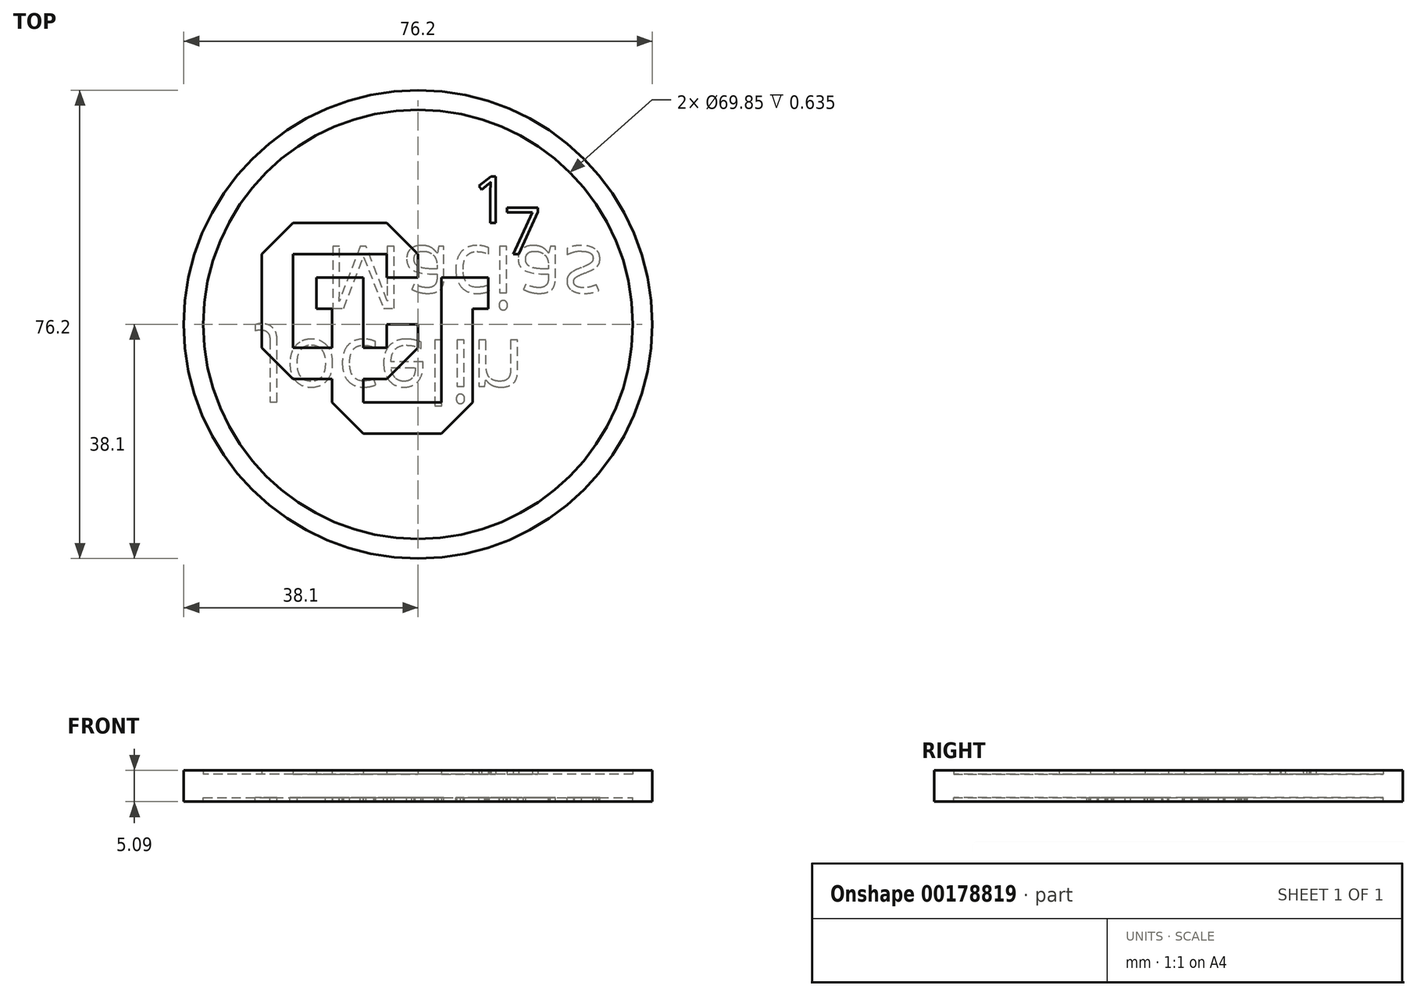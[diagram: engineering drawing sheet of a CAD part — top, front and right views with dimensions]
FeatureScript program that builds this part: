
annotation { "Feature Type Name" : "Feature", "Feature Type Description" : "" }
export const myFeature = defineFeature(function(context is Context, id is Id, definition is map)
    precondition{}
    {
        {
            var Q0;
            Q0=qCreatedBy(makeId("Top.planeOp"),FACE);
            var sketch = newSketch(context, id + "F0", { "sketchPlane" : qUnion([Q0])});
            skCircle(sketch, "E0", {"center": v(0, 0) * mm, "radius": 38.1 * mm});
            skSolve(sketch);
        }
        {
            var Q0;
            Q0=makeQuery(id+"F0.imprint","IMPRINT",FACE,{"disambiguationData":[TD([[makeQuery(id+"F0.imprint","IMPRINT",EDGE,{"derivedFrom":sQuery(id+"F0.wireOp",EDGE,"E0")}),1.0]])]});
            extrude(context, id + "F1", {"entities" : qUnion([Q0]), "depth" : 3.8 * mm});
        }
        {
            var Q0;
            Q0=makeQuery(id+"F1.opExtrude","CAP_FACE",FACE,{"disambiguationData":[OSD([sQuery(id+"F0.wireOp",EDGE,"E0")])],"isStart":false});
            var sketch = newSketch(context, id + "F2", { "sketchPlane" : qUnion([Q0])});
            skLineSegment(sketch, "E1", {"start": v(0, 0) * mm, "end": v(0, -3.81) * mm});
            skLineSegment(sketch, "E2", {"start": v(0, -3.81) * mm, "end": v(-5.08, -8.9) * mm});
            skLineSegment(sketch, "E3", {"start": v(-5.08, -8.9) * mm, "end": v(-8.9, -8.9) * mm});
            skLineSegment(sketch, "E4", {"start": v(-20.32, -8.9) * mm, "end": v(-25.4, -3.81) * mm});
            skLineSegment(sketch, "E5", {"start": v(-25.4, -3.81) * mm, "end": v(-25.4, 11.43) * mm});
            skLineSegment(sketch, "E6", {"start": v(-25.4, 11.43) * mm, "end": v(-20.32, 16.5) * mm});
            skLineSegment(sketch, "E7", {"start": v(-20.32, 16.51) * mm, "end": v(-5.08, 16.51) * mm});
            skLineSegment(sketch, "E8", {"start": v(-5.08, 16.51) * mm, "end": v(0, 11.43) * mm});
            skLineSegment(sketch, "E9", {"start": v(0, 11.43) * mm, "end": v(0, 7.62) * mm});
            skLineSegment(sketch, "E10", {"start": v(0, 7.62) * mm, "end": v(-5.08, 7.62) * mm});
            skLineSegment(sketch, "E11", {"start": v(-5.08, 7.62) * mm, "end": v(-5.08, 11.43) * mm});
            skLineSegment(sketch, "E12", {"start": v(-5.08, 11.43) * mm, "end": v(-20.32, 11.43) * mm});
            skLineSegment(sketch, "E13", {"start": v(-20.32, 11.43) * mm, "end": v(-20.32, -3.81) * mm});
            skLineSegment(sketch, "E14", {"start": v(-20.32, -3.81) * mm, "end": v(-13.97, -3.81) * mm});
            skLineSegment(sketch, "E15", {"start": v(-5.08, -3.81) * mm, "end": v(-5.08, 0) * mm});
            skLineSegment(sketch, "E16", {"start": v(-5.08, 0) * mm, "end": v(0, 0) * mm});
            skLineSegment(sketch, "E17", {"start": v(-8.9, -3.81) * mm, "end": v(-8.9, 7.62) * mm});
            skLineSegment(sketch, "E18", {"start": v(-8.9, 7.62) * mm, "end": v(-16.5, 7.62) * mm});
            skLineSegment(sketch, "E19", {"start": v(-16.5, 7.62) * mm, "end": v(-16.5, 2.54) * mm});
            skLineSegment(sketch, "E20", {"start": v(-16.51, 2.54) * mm, "end": v(-13.97, 2.54) * mm});
            skLineSegment(sketch, "E21", {"start": v(-13.97, 2.54) * mm, "end": v(-13.97, -3.8) * mm});
            skLineSegment(sketch, "E22.trimOffspring", {"start": v(-8.9, -3.81) * mm, "end": v(-5.08, -3.81) * mm});
            skLineSegment(sketch, "E23", {"start": v(-13.97, -12.7) * mm, "end": v(-13.97, -8.9) * mm});
            skLineSegment(sketch, "E24", {"start": v(-13.97, -12.7) * mm, "end": v(-8.9, -17.78) * mm});
            skLineSegment(sketch, "E25", {"start": v(-8.9, -17.78) * mm, "end": v(3.8, -17.78) * mm});
            skLineSegment(sketch, "E26", {"start": v(3.8, -17.78) * mm, "end": v(8.89, -12.7) * mm});
            skLineSegment(sketch, "E27", {"start": v(8.89, -12.7) * mm, "end": v(8.9, 2.54) * mm});
            skLineSegment(sketch, "E28", {"start": v(8.9, 2.54) * mm, "end": v(11.43, 2.54) * mm});
            skLineSegment(sketch, "E29", {"start": v(11.43, 2.54) * mm, "end": v(11.43, 7.62) * mm});
            skLineSegment(sketch, "E30", {"start": v(11.43, 7.62) * mm, "end": v(3.8, 7.62) * mm});
            skLineSegment(sketch, "E31", {"start": v(3.8, 7.62) * mm, "end": v(3.8, -12.7) * mm});
            skLineSegment(sketch, "E32", {"start": v(3.8, -12.7) * mm, "end": v(-8.9, -12.7) * mm});
            skLineSegment(sketch, "E33", {"start": v(-8.9, -12.7) * mm, "end": v(-8.9, -8.9) * mm});
            skLineSegment(sketch, "E34.trimOffspring", {"start": v(-13.97, -8.9) * mm, "end": v(-20.32, -8.9) * mm});
            skCircle(sketch, "E35", {"center": v(0, 0) * mm, "radius": 38.1 * mm});
            skCircle(sketch, "E36.0", {"center": v(0, 0) * mm, "radius": 34.93 * mm});
            skText(sketch, "E37", { "text": "1\n", "fontName": "OpenSans-Regular.ttf"});
            skText(sketch, "E38", { "text": "7\n", "fontName": "OpenSans-Regular.ttf"});
            const initialGuessF2  = {"E37": [0.0089, 0.0165, 1, 0, 0.00762], "E38": [0.01397, 0.01143, 1, 0, 0.00762]};
            skSetInitialGuess(sketch, initialGuessF2);
            skSolve(sketch);
        }
        {
            var Q0;
            Q0=qSketchRegion(id+"F2",true);
            var Q1;
            Q1=makeQuery(id+"F2.imprint","IMPRINT",FACE,{"disambiguationData":[TD([[makeQuery(id+"F2.imprint","IMPRINT",EDGE,{"derivedFrom":sQuery(id+"F2.wireOp",EDGE,"06a9ea4b-25a0-40bb-ae41-652813a8379c.sketch_text.stroke-0")}),-1.0]])]});
            var Q2;
            Q2=makeQuery(id+"F2.imprint","IMPRINT",FACE,{"disambiguationData":[TD([[makeQuery(id+"F2.imprint","IMPRINT",EDGE,{"derivedFrom":sQuery(id+"F2.wireOp",EDGE,"5a37e26c-5f2a-4299-bdd1-32ef89c17c20.sketch_text.stroke-0")}),-1.0]])]});
            var Q3;
            Q3=makeQuery(id+"F2.imprint","IMPRINT",FACE,{"disambiguationData":[TD([[makeQuery(id+"F2.imprint","IMPRINT",EDGE,{"derivedFrom":sQuery(id+"F2.wireOp",EDGE,"899a0aec-380f-455c-b9af-3a8c948fcc07.sketch_text.stroke-0")}),-1.0]])]});
            var Q4;
            Q4=makeQuery(id+"F2.imprint","IMPRINT",FACE,{"disambiguationData":[TD([[makeQuery(id+"F2.imprint","IMPRINT",EDGE,{"derivedFrom":sQuery(id+"F2.wireOp",EDGE,"097ffee6-68a2-43e3-9acb-eec1a9da6394.sketch_text.stroke-0")}),-1.0]])]});
            var Q5;
            Q5=makeQuery(id+"F2.imprint","IMPRINT",FACE,{"disambiguationData":[TD([[makeQuery(id+"F2.imprint","IMPRINT",EDGE,{"derivedFrom":sQuery(id+"F2.wireOp",EDGE,"E1")}),-1.0]])]});
            var Q6;
            Q6=makeQuery(id+"F2.imprint","IMPRINT",FACE,{"disambiguationData":[TD([[makeQuery(id+"F2.imprint","IMPRINT",EDGE,{"derivedFrom":sQuery(id+"F2.wireOp",EDGE,"d49a6b62-95a8-4d28-aa0c-83bd3f69134a.sketch_text.stroke-0")}),-1.0]])]});
            var Q7;
            Q7=makeQuery(id+"F2.imprint","IMPRINT",FACE,{"disambiguationData":[TD([[makeQuery(id+"F2.imprint","IMPRINT",EDGE,{"derivedFrom":sQuery(id+"F2.wireOp",EDGE,"d49a6b62-95a8-4d28-aa0c-83bd3f69134a.sketch_text.stroke-20")}),-1.0]])]});
            var Q8;
            Q8=makeQuery(id+"F2.imprint","IMPRINT",FACE,{"disambiguationData":[TD([[makeQuery(id+"F2.imprint","IMPRINT",EDGE,{"derivedFrom":sQuery(id+"F2.wireOp",EDGE,"d49a6b62-95a8-4d28-aa0c-83bd3f69134a.sketch_text.stroke-36")}),-1.0]])]});
            var Q9;
            Q9=makeQuery(id+"F2.imprint","IMPRINT",FACE,{"disambiguationData":[TD([[makeQuery(id+"F2.imprint","IMPRINT",EDGE,{"derivedFrom":sQuery(id+"F2.wireOp",EDGE,"d49a6b62-95a8-4d28-aa0c-83bd3f69134a.sketch_text.stroke-45")}),-1.0]])]});
            var Q10;
            Q10=makeQuery(id+"F2.imprint","IMPRINT",FACE,{"disambiguationData":[TD([[makeQuery(id+"F2.imprint","IMPRINT",EDGE,{"derivedFrom":sQuery(id+"F2.wireOp",EDGE,"E37.sketch_text.stroke-0")}),-1.0]])]});
            var Q11;
            Q11=makeQuery(id+"F2.imprint","IMPRINT",FACE,{"disambiguationData":[TD([[makeQuery(id+"F2.imprint","IMPRINT",EDGE,{"derivedFrom":sQuery(id+"F2.wireOp",EDGE,"E38.sketch_text.stroke-0")}),-1.0]])]});
            extrude(context, id + "F3", {"entities" : qUnion([Q0, Q1, Q2, Q3, Q4, Q5, Q6, Q7, Q8, Q9, Q10, Q11]), "operationType" : NewBodyOperationType.ADD, "depth" : 0.64 * mm});
        }
        {
            var Q0;
            Q0=makeQuery(id+"F1.opExtrude","CAP_FACE",FACE,{"disambiguationData":[OSD([sQuery(id+"F0.wireOp",EDGE,"E0")])],"isStart":true});
            var sketch = newSketch(context, id + "F4", { "sketchPlane" : qUnion([Q0])});
            skCircle(sketch, "E39", {"center": v(0, 0) * mm, "radius": 38.1 * mm});
            skCircle(sketch, "E40", {"center": v(0, 0) * mm, "radius": 34.93 * mm});
            skText(sketch, "E41", { "text": "Jocelin\n", "fontName": "OpenSans-Regular.ttf"});
            skText(sketch, "E42", { "text": "Macias\n", "fontName": "OpenSans-Regular.ttf"});
            const initialGuessF4  = {"E41": [-0.0254, 0.00254, 1, 0, 0.01016], "E42": [-0.01524, -0.0127, 1, 0, 0.01016]};
            skSetInitialGuess(sketch, initialGuessF4);
            skSolve(sketch);
        }
        {
            var Q0;
            Q0=qSketchRegion(id+"F4",true);
            var Q1;
            Q1=makeQuery(id+"F4.imprint","IMPRINT",FACE,{"disambiguationData":[TD([[makeQuery(id+"F4.imprint","IMPRINT",EDGE,{"derivedFrom":sQuery(id+"F4.wireOp",EDGE,"65399ead-6b07-49af-8cc2-ccb61a4753ff.sketch_text.stroke-46")}),-1.0]])]});
            var Q2;
            Q2=makeQuery(id+"F4.imprint","IMPRINT",FACE,{"disambiguationData":[TD([[makeQuery(id+"F4.imprint","IMPRINT",EDGE,{"derivedFrom":sQuery(id+"F4.wireOp",EDGE,"65399ead-6b07-49af-8cc2-ccb61a4753ff.sketch_text.stroke-50")}),-1.0]])]});
            var Q3;
            Q3=makeQuery(id+"F4.imprint","IMPRINT",FACE,{"disambiguationData":[TD([[makeQuery(id+"F4.imprint","IMPRINT",EDGE,{"derivedFrom":sQuery(id+"F4.wireOp",EDGE,"65399ead-6b07-49af-8cc2-ccb61a4753ff.sketch_text.stroke-33")}),-1.0]])]});
            var Q4;
            Q4=makeQuery(id+"F4.imprint","IMPRINT",FACE,{"disambiguationData":[TD([[makeQuery(id+"F4.imprint","IMPRINT",EDGE,{"derivedFrom":sQuery(id+"F4.wireOp",EDGE,"65399ead-6b07-49af-8cc2-ccb61a4753ff.sketch_text.stroke-15")}),-1.0]])]});
            var Q5;
            Q5=makeQuery(id+"F4.imprint","IMPRINT",FACE,{"disambiguationData":[TD([[makeQuery(id+"F4.imprint","IMPRINT",EDGE,{"derivedFrom":sQuery(id+"F4.wireOp",EDGE,"65399ead-6b07-49af-8cc2-ccb61a4753ff.sketch_text.stroke-0")}),-1.0]])]});
            var Q6;
            Q6=makeQuery(id+"F4.imprint","IMPRINT",FACE,{"disambiguationData":[TD([[makeQuery(id+"F4.imprint","IMPRINT",EDGE,{"derivedFrom":sQuery(id+"F4.wireOp",EDGE,"65399ead-6b07-49af-8cc2-ccb61a4753ff.sketch_text.stroke-58")}),-1.0]])]});
            var Q7;
            Q7=makeQuery(id+"F4.imprint","IMPRINT",FACE,{"disambiguationData":[TD([[makeQuery(id+"F4.imprint","IMPRINT",EDGE,{"derivedFrom":sQuery(id+"F4.wireOp",EDGE,"GNh5wkv0-m4cR-m8Q0-8Bcc-Us7GIQ0LKi4J")}),1.0]])]});
            var Q8;
            Q8=makeQuery(id+"F4.imprint","IMPRINT",FACE,{"disambiguationData":[TD([[makeQuery(id+"F4.imprint","IMPRINT",EDGE,{"derivedFrom":sQuery(id+"F4.wireOp",EDGE,"87599fc1-b51d-4faf-a010-de93aa910fde0.MirrorC")}),-1.0]])]});
            var Q9;
            Q9=makeQuery(id+"F4.imprint","IMPRINT",FACE,{"disambiguationData":[TD([[makeQuery(id+"F4.imprint","IMPRINT",EDGE,{"derivedFrom":sQuery(id+"F4.wireOp",EDGE,"KY91P05g-cfxj-tiq1-HTrz-ahMGwcPuLG5K")}),1.0]])]});
            var Q10;
            Q10=makeQuery(id+"F4.imprint","IMPRINT",FACE,{"disambiguationData":[TD([[makeQuery(id+"F4.imprint","IMPRINT",EDGE,{"derivedFrom":sQuery(id+"F4.wireOp",EDGE,"RqR0lVDM-6pCL-N6dA-WNhf-UV2zKxsPLnjl")}),1.0]])]});
            var Q11;
            Q11=makeQuery(id+"F4.imprint","IMPRINT",FACE,{"disambiguationData":[TD([[makeQuery(id+"F4.imprint","IMPRINT",EDGE,{"derivedFrom":sQuery(id+"F4.wireOp",EDGE,"2c46f6d1-9486-4298-9521-c78d2df75ac9.sketch_text.stroke-0")}),-1.0]])]});
            var Q12;
            Q12=makeQuery(id+"F4.imprint","IMPRINT",FACE,{"disambiguationData":[TD([[makeQuery(id+"F4.imprint","IMPRINT",EDGE,{"derivedFrom":sQuery(id+"F4.wireOp",EDGE,"2c46f6d1-9486-4298-9521-c78d2df75ac9.sketch_text.stroke-15")}),-1.0]])]});
            var Q13;
            Q13=makeQuery(id+"F4.imprint","IMPRINT",FACE,{"disambiguationData":[TD([[makeQuery(id+"F4.imprint","IMPRINT",EDGE,{"derivedFrom":sQuery(id+"F4.wireOp",EDGE,"2c46f6d1-9486-4298-9521-c78d2df75ac9.sketch_text.stroke-33")}),-1.0]])]});
            var Q14;
            Q14=makeQuery(id+"F4.imprint","IMPRINT",FACE,{"disambiguationData":[TD([[makeQuery(id+"F4.imprint","IMPRINT",EDGE,{"derivedFrom":sQuery(id+"F4.wireOp",EDGE,"2c46f6d1-9486-4298-9521-c78d2df75ac9.sketch_text.stroke-50")}),-1.0]])]});
            var Q15;
            Q15=makeQuery(id+"F4.imprint","IMPRINT",FACE,{"disambiguationData":[TD([[makeQuery(id+"F4.imprint","IMPRINT",EDGE,{"derivedFrom":sQuery(id+"F4.wireOp",EDGE,"2c46f6d1-9486-4298-9521-c78d2df75ac9.sketch_text.stroke-77")}),-1.0]])]});
            var Q16;
            Q16=makeQuery(id+"F4.imprint","IMPRINT",FACE,{"disambiguationData":[TD([[makeQuery(id+"F4.imprint","IMPRINT",EDGE,{"derivedFrom":sQuery(id+"F4.wireOp",EDGE,"E41.sketch_text.stroke-10")}),-1.0]])]});
            var Q17;
            Q17=makeQuery(id+"F4.imprint","IMPRINT",FACE,{"disambiguationData":[TD([[makeQuery(id+"F4.imprint","IMPRINT",EDGE,{"derivedFrom":sQuery(id+"F4.wireOp",EDGE,"E41.sketch_text.stroke-27")}),-1.0]])]});
            var Q18;
            Q18=makeQuery(id+"F4.imprint","IMPRINT",FACE,{"disambiguationData":[TD([[makeQuery(id+"F4.imprint","IMPRINT",EDGE,{"derivedFrom":sQuery(id+"F4.wireOp",EDGE,"E41.sketch_text.stroke-0")}),-1.0]])]});
            var Q19;
            Q19=makeQuery(id+"F4.imprint","IMPRINT",FACE,{"disambiguationData":[TD([[makeQuery(id+"F4.imprint","IMPRINT",EDGE,{"derivedFrom":sQuery(id+"F4.wireOp",EDGE,"E41.sketch_text.stroke-42")}),-1.0]])]});
            var Q20;
            Q20=makeQuery(id+"F4.imprint","IMPRINT",FACE,{"disambiguationData":[TD([[makeQuery(id+"F4.imprint","IMPRINT",EDGE,{"derivedFrom":sQuery(id+"F4.wireOp",EDGE,"E41.sketch_text.stroke-61")}),-1.0]])]});
            var Q21;
            Q21=makeQuery(id+"F4.imprint","IMPRINT",FACE,{"disambiguationData":[TD([[makeQuery(id+"F4.imprint","IMPRINT",EDGE,{"derivedFrom":sQuery(id+"F4.wireOp",EDGE,"E41.sketch_text.stroke-65")}),-1.0]])]});
            var Q22;
            Q22=makeQuery(id+"F4.imprint","IMPRINT",FACE,{"disambiguationData":[TD([[makeQuery(id+"F4.imprint","IMPRINT",EDGE,{"derivedFrom":sQuery(id+"F4.wireOp",EDGE,"E41.sketch_text.stroke-69")}),-1.0]])]});
            var Q23;
            Q23=makeQuery(id+"F4.imprint","IMPRINT",FACE,{"disambiguationData":[TD([[makeQuery(id+"F4.imprint","IMPRINT",EDGE,{"derivedFrom":sQuery(id+"F4.wireOp",EDGE,"E42.sketch_text.stroke-0")}),-1.0]])]});
            var Q24;
            Q24=makeQuery(id+"F4.imprint","IMPRINT",FACE,{"disambiguationData":[TD([[makeQuery(id+"F4.imprint","IMPRINT",EDGE,{"derivedFrom":sQuery(id+"F4.wireOp",EDGE,"E42.sketch_text.stroke-18")}),-1.0]])]});
            var Q25;
            Q25=makeQuery(id+"F4.imprint","IMPRINT",FACE,{"disambiguationData":[TD([[makeQuery(id+"F4.imprint","IMPRINT",EDGE,{"derivedFrom":sQuery(id+"F4.wireOp",EDGE,"E42.sketch_text.stroke-45")}),-1.0]])]});
            var Q26;
            Q26=makeQuery(id+"F4.imprint","IMPRINT",FACE,{"disambiguationData":[TD([[makeQuery(id+"F4.imprint","IMPRINT",EDGE,{"derivedFrom":sQuery(id+"F4.wireOp",EDGE,"E42.sketch_text.stroke-60")}),-1.0]])]});
            var Q27;
            Q27=makeQuery(id+"F4.imprint","IMPRINT",FACE,{"disambiguationData":[TD([[makeQuery(id+"F4.imprint","IMPRINT",EDGE,{"derivedFrom":sQuery(id+"F4.wireOp",EDGE,"E42.sketch_text.stroke-64")}),-1.0]])]});
            var Q28;
            Q28=makeQuery(id+"F4.imprint","IMPRINT",FACE,{"disambiguationData":[TD([[makeQuery(id+"F4.imprint","IMPRINT",EDGE,{"derivedFrom":sQuery(id+"F4.wireOp",EDGE,"E42.sketch_text.stroke-72")}),-1.0]])]});
            var Q29;
            Q29=makeQuery(id+"F4.imprint","IMPRINT",FACE,{"disambiguationData":[TD([[makeQuery(id+"F4.imprint","IMPRINT",EDGE,{"derivedFrom":sQuery(id+"F4.wireOp",EDGE,"E42.sketch_text.stroke-99")}),-1.0]])]});
            var Q30;
            Q30=makeQuery(id+"F4.imprint","IMPRINT",FACE,{"disambiguationData":[TD([[makeQuery(id+"F4.imprint","IMPRINT",EDGE,{"derivedFrom":sQuery(id+"F4.wireOp",EDGE,"E41.sketch_text.stroke-77")}),-1.0]])]});
            extrude(context, id + "F5", {"entities" : qUnion([Q0, Q1, Q2, Q3, Q4, Q5, Q6, Q7, Q8, Q9, Q10, Q11, Q12, Q13, Q14, Q15, Q16, Q17, Q18, Q19, Q20, Q21, Q22, Q23, Q24, Q25, Q26, Q27, Q28, Q29, Q30]), "operationType" : NewBodyOperationType.ADD, "depth" : 0.64 * mm});
        }
    });
